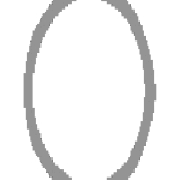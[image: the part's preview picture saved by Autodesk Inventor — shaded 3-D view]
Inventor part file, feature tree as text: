
AUTODESK INVENTOR PART (.ipt)
format: ipt  version: 2021 (Build 250183000, 183)  size: 113,152 bytes
history: native  units: in
note: dims shown in document units (in); Inventor stores cm internally (conversion verified against a paired STEP export)
features: other x4, sketch x3, plane x1
ambient origin geometry x8: Origin, YZ Plane, XZ Plane, XY Plane, X Axis, Y Axis, Z Axis, Center Point
bodies: Solid1 (feature_tree), Body (feature_tree)
feature tree (8):
  other  "Driven Length"
  other  "Frame Generator"
  other  "Start Plane"
  other  "End Plane"
  sketch  "Sketch"  dims[d2=9.0139in d4=-0.0in d5=9.0139in d6=0.12in d7=0.0in d8=90.0deg d9=9.0139in]
  sketch  "Sketch2"  dims[d0=1.0in]
  plane  "Work Plane3"
  sketch  "Sketch3"  dims[d1=0.065in]
